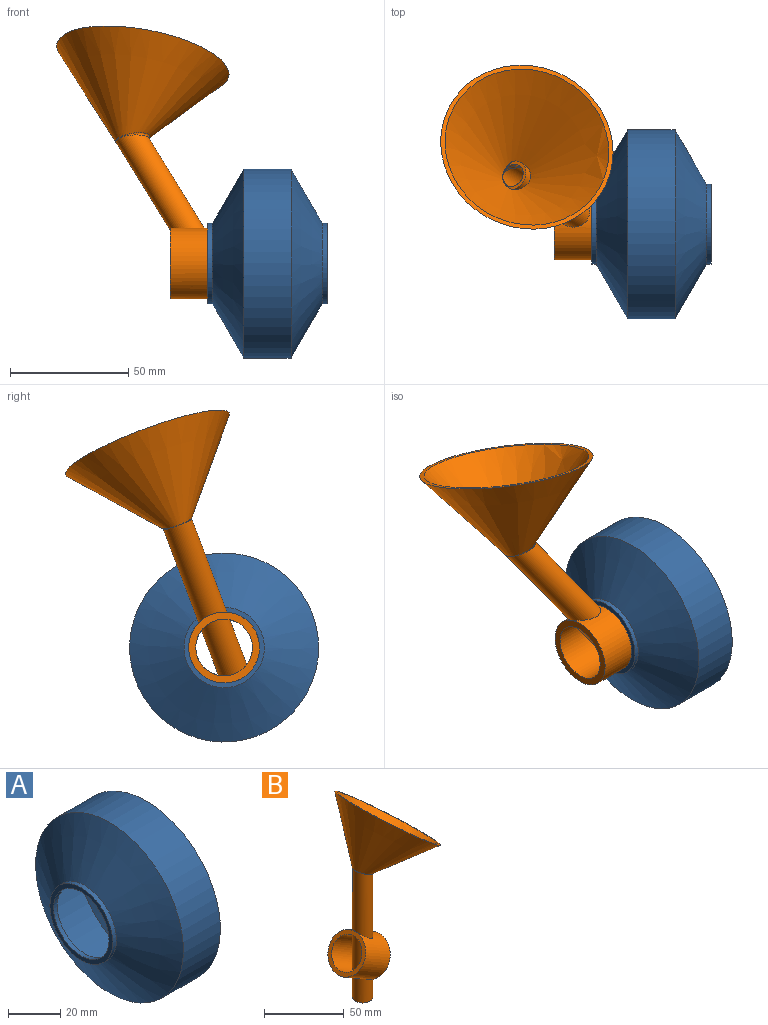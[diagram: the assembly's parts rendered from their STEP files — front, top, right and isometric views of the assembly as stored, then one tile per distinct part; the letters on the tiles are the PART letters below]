
ASSEMBLY  parts=2 mates=1
PART A: 12 faces, bbox 50.6x80x80 mm
  f0: cylinder r=38.6mm len=77.2mm, axis (-1,0,0), area 4682.6mm2, adj f1,f7
  f1: cone r=15mm half-angle=60deg, axis (1,0,0), area 4588.8mm2, adj f0,f2
  f2: cylinder r=15mm len=30mm, axis (-1,0,0), area 188.5mm2, adj f1,f3
  f3: plane 34x34mm, normal (-1,0,0), area 201.1mm2, adj f2,f4
  f4: cylinder r=17mm len=34mm, axis (-1,0,0), area 213.6mm2, adj f3,f5
  f5: cone r=40mm half-angle=60deg, axis (1,0,0), area 4755.8mm2, adj f4,f6
  f6: cylinder r=40mm len=80mm, axis (-1,0,0), area 5026.5mm2, adj f5,f11
  f7: cone r=15mm half-angle=60deg, axis (-1,0,0), area 4588.8mm2, adj f0,f8
  f8: cylinder r=15mm len=30mm, axis (1,0,0), area 188.5mm2, adj f7,f9
  f9: plane 34x34mm, normal (1,0,0), area 201.1mm2, adj f8,f10
  f10: cylinder r=17mm len=34mm, axis (1,0,0), area 213.6mm2, adj f9,f11
  f11: cone r=40mm half-angle=60deg, axis (-1,0,0), area 4755.8mm2, adj f6,f10
PART B: 28 faces, bbox 74.1x76.2x152.2 mm
  f0: cylinder r=5mm len=53.03mm, axis (0,0,1), area 1474.5mm2, adj f1,f25,f26,f27
  f1: cone r=3.83mm half-angle=50deg, axis (-0.64,0,-0.77), area 0.3mm2, adj f0,f2,f3,f26
  f2: cylinder r=4.95mm len=8.76mm, axis (0,0,1), area 12.9mm2, adj f1,f3,f26
  f3: cone r=35.21mm half-angle=40deg, axis (0.64,0,0.77), area 3.2mm2, adj f1,f2,f4,f5,f6,f25
  f4: cylinder r=4.95mm len=8.76mm, axis (0,0,1), area 12.9mm2, adj f3,f25,f26
  f5: cylinder r=4.95mm len=3.68mm, axis (0,0,1), area 0.4mm2, adj f3,f26
  f6: cylinder r=5mm len=10mm, axis (0,0,1), area 65.9mm2, adj f3,f7
  f7: plane 14.96x13.56mm, normal (0,0,1), area 30.8mm2, adj f6,f8,f9
  f8: cylinder r=6.4mm len=12.8mm, axis (0,0,1), area 40.6mm2, adj f7,f9
  f9: cone r=35.21mm half-angle=40deg, axis (0.64,0,0.77), area 5877.3mm2, adj f7,f8,f10
  f10: plane 74.08x56.75mm, normal (0.64,0,0.77), area 414.9mm2, adj f9,f11
  f11: cone r=4.9mm half-angle=40deg, axis (0.64,0,0.77), area 6467.1mm2, adj f10,f12
  f12: bspline ~13.63x13.34mm, area 21.3mm2, adj f11,f13
  f13: cylinder r=6.4mm len=53.84mm, axis (0,0,1), area 1891.5mm2, adj f12,f14
  f14: cylinder r=15mm len=38.48mm, axis (-0.87,0,0.5), area 2122.7mm2, adj f13,f15,f23,f24
  f15: cylinder r=6.4mm len=50.09mm, axis (0,0,1), area 1736.5mm2, adj f14,f16,f17,f23
  f16: cylinder r=12mm len=33.65mm, axis (-0.87,0,0.5), area 1624.5mm2, adj f15,f23,f24
  f17: plane 12.8x12.8mm, normal (0,0,-1), area 50.1mm2, adj f15,f18
  f18: cylinder r=5mm len=49.28mm, axis (0,0,1), area 1371.6mm2, adj f17,f19,f20,f21,f22
  f19: cylinder r=12mm len=10mm, axis (-0.87,0,0.5), area 66.8mm2, adj f18,f21
  f20: cylinder r=15mm len=10mm, axis (-0.87,0,0.5), area 48.8mm2, adj f18,f21
  f21: plane 10x3.44mm, normal (0.87,0,-0.5), area 29.5mm2, adj f18,f19,f20
  f22: cylinder r=12mm len=10.55mm, axis (-0.87,0,0.5), area 92.8mm2, adj f18
  f23: plane 30.05x24.81mm, normal (0.87,0,-0.5), area 215.9mm2, adj f14,f15,f16
  f24: plane 30x25.98mm, normal (-0.87,0,0.5), area 254.5mm2, adj f14,f16
  f25: cone r=3.83mm half-angle=50deg, axis (-0.64,0,-0.77), area 0.3mm2, adj f0,f3,f4,f26
  f26: cone r=4.9mm half-angle=40deg, axis (0.64,0,0.77), area 1.1mm2, adj f0,f1,f2,f4,f5,f25
  f27: cylinder r=15mm len=10.43mm, axis (-0.87,0,0.5), area 92mm2, adj f0
PLACE A rot(axis=(1,0,0),146.3deg) t=(2.5,0,0)mm
PLACE B rot(axis=(-0.56,-0.82,0.15),36.3deg) t=(-56.13,20.62,54.67)mm fixed
MATE cylindrical B.f14 <-> A.f0  axis (-1,0,0) through (-26.13,0,0)mm
